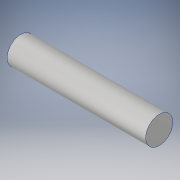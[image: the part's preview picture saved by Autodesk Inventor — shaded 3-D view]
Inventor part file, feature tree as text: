
AUTODESK INVENTOR PART (.ipt)
format: ipt  version: 2019 (Build 230136000, 136)  size: 92,672 bytes
history: native  units: mm
features: other x1, extrude x1, sketch x1
ambient origin geometry x8: Origin, YZ Plane, XZ Plane, XY Plane, X Axis, Y Axis, Z Axis, Center Point
bodies: Body1 (feature_tree)
feature tree (3):
  other  "Bryła1"
  extrude  "Wyciągnięcie proste1"  Depth=2.5mm
  sketch  "Szkic1"
